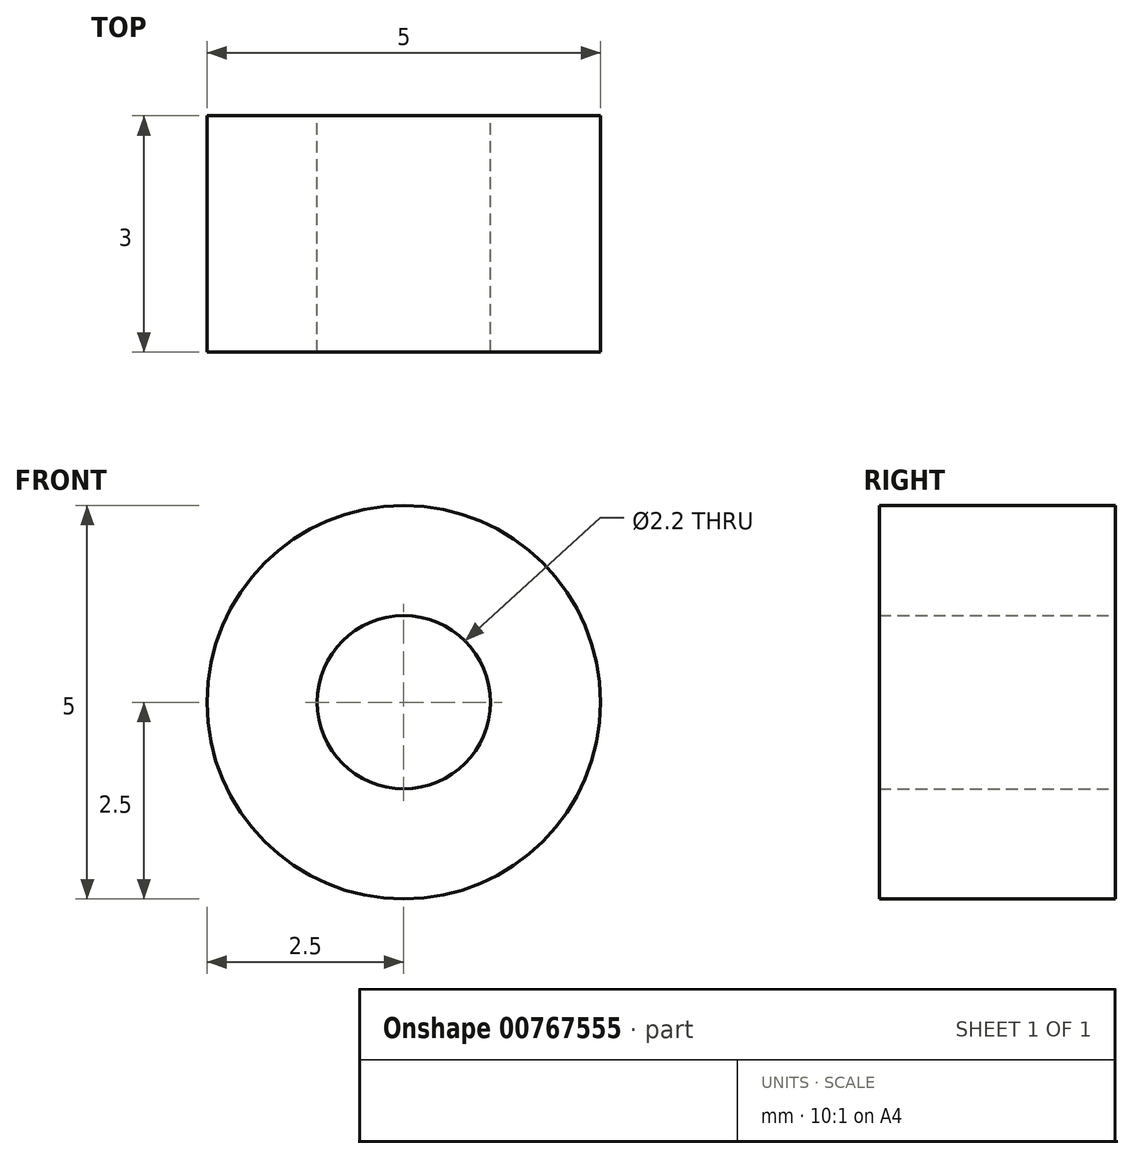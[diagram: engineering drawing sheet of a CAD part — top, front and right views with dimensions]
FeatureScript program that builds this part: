
annotation { "Feature Type Name" : "Feature", "Feature Type Description" : "" }
export const myFeature = defineFeature(function(context is Context, id is Id, definition is map)
    precondition{}
    {
        {
            var Q0;
            Q0=qCreatedBy(makeId("Front.planeOp"),FACE);
            var sketch = newSketch(context, id + "F0", { "sketchPlane" : qUnion([Q0])});
            skCircle(sketch, "E0", {"center": v(0, 0) * mm, "radius": 2.5 * mm});
            skCircle(sketch, "E1", {"center": v(0, 0) * mm, "radius": 1.1 * mm});
            skSolve(sketch);
        }
        {
            var Q0;
            Q0=makeQuery(id+"F0.imprint","IMPRINT",FACE,{"disambiguationData":[TD([[makeQuery(id+"F0.imprint","IMPRINT",EDGE,{"derivedFrom":sQuery(id+"F0.wireOp",EDGE,"E0")}),1.0]])]});
            extrude(context, id + "F1", {"entities" : qUnion([Q0]), "depth" : 3 * mm, "offsetDistance" : 25 * mm});
        }
    });
